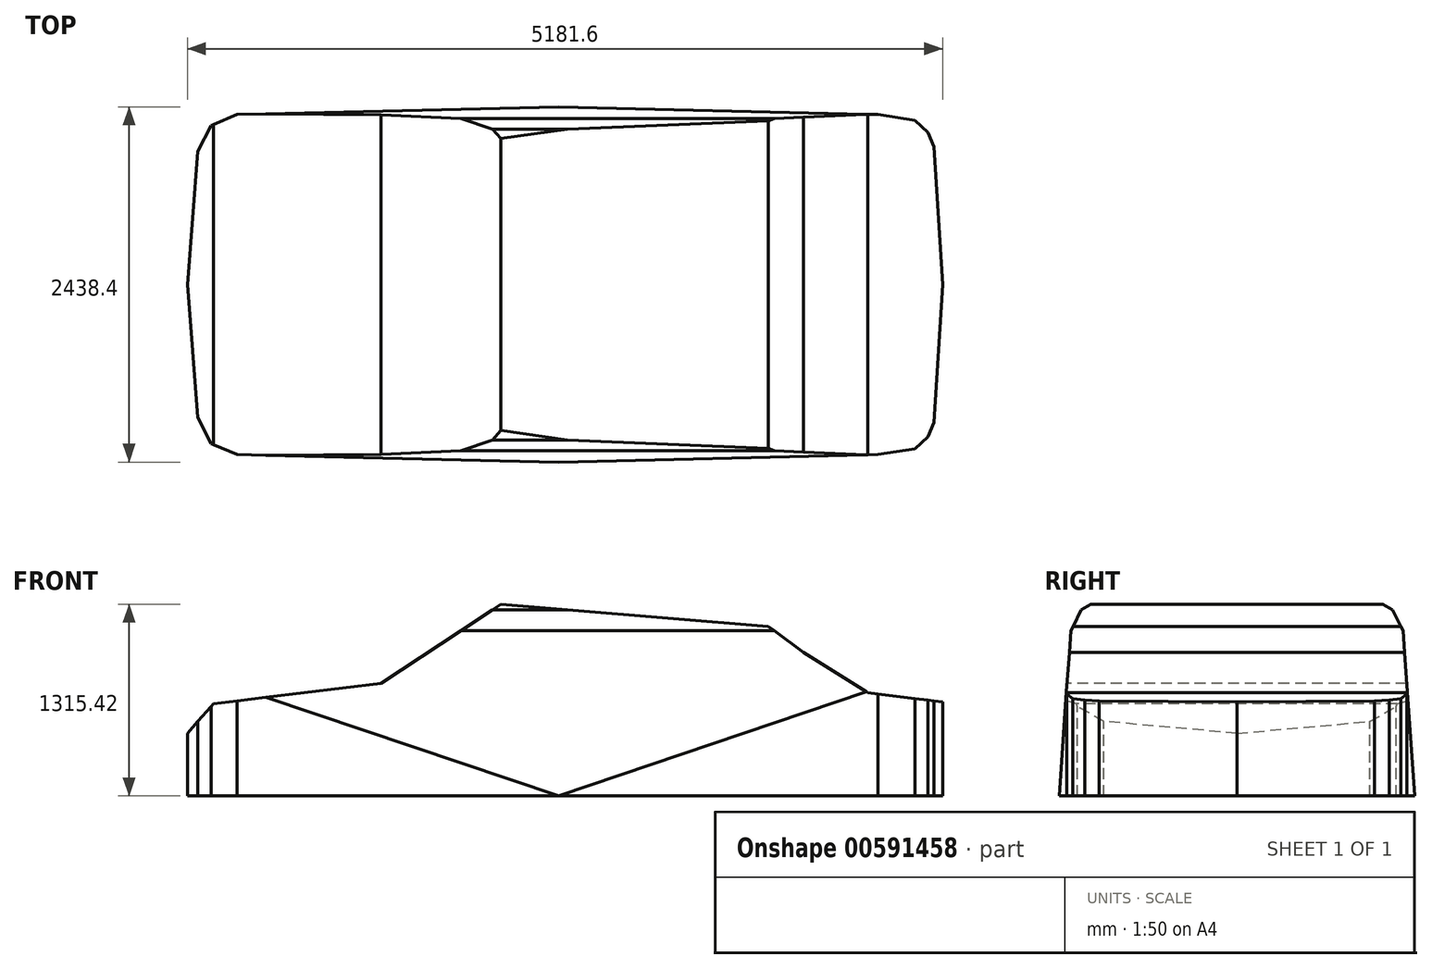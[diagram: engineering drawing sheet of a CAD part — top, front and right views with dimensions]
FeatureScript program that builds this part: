
annotation { "Feature Type Name" : "Feature", "Feature Type Description" : "" }
export const myFeature = defineFeature(function(context is Context, id is Id, definition is map)
    precondition{}
    {
        {
            var Q0;
            Q0=qCreatedBy(makeId("Top.planeOp"),FACE);
            var sketch = newSketch(context, id + "F0", { "sketchPlane" : qUnion([Q0])});
            skLineSegment(sketch, "E0.bottom", {"start": v(-2577.75, 1480) * mm, "end": v(2603.85, 1480) * mm});
            skLineSegment(sketch, "E0.top", {"start": v(-2577.75, -958.4) * mm, "end": v(2603.85, -958.4) * mm});
            skLineSegment(sketch, "E0.left", {"start": v(-2577.75, 1480) * mm, "end": v(-2577.75, -958.4) * mm});
            skLineSegment(sketch, "E0.right", {"start": v(2603.85, 1480) * mm, "end": v(2603.85, -958.4) * mm});
            skSolve(sketch);
        }
        {
            var Q0;
            Q0=makeQuery(id+"F0.imprint","IMPRINT",FACE,{"disambiguationData":[TD([[makeQuery(id+"F0.imprint","IMPRINT",EDGE,{"derivedFrom":sQuery(id+"F0.wireOp",EDGE,"E0.bottom")}),-1.0]])]});
            extrude(context, id + "F1", {"entities" : qUnion([Q0]), "depth" : 1524 * mm, "offsetDistance" : 25.4 * mm});
        }
        {
            var Q0;
            Q0=makeQuery(id+"F1.opExtrude","SWEPT_FACE",FACE,{"disambiguationData":[OSD([sQuery(id+"F0.wireOp",EDGE,"E0.top")])]});
            var sketch = newSketch(context, id + "F2", { "sketchPlane" : qUnion([Q0])});
            skLineSegment(sketch, "E1", {"start": v(2603.85, 644.82) * mm, "end": v(2603.85, 0) * mm});
            skLineSegment(sketch, "E2", {"start": v(2603.85, 0) * mm, "end": v(-2577.75, 0) * mm});
            skLineSegment(sketch, "E3", {"start": v(-2577.75, 0) * mm, "end": v(-2577.75, 429.72) * mm});
            skLineSegment(sketch, "E4", {"start": v(-2577.75, 429.72) * mm, "end": v(-2400.46, 632.17) * mm});
            skLineSegment(sketch, "E5", {"start": v(-2400.46, 632.17) * mm, "end": v(-1249.06, 771.35) * mm});
            skLineSegment(sketch, "E6", {"start": v(-1249.06, 771.35) * mm, "end": v(-426.63, 1315.42) * mm});
            skLineSegment(sketch, "E7", {"start": v(-426.63, 1315.42) * mm, "end": v(1408.01, 1163.58) * mm});
            skLineSegment(sketch, "E8", {"start": v(1408.01, 1163.58) * mm, "end": v(1648.42, 986.44) * mm});
            skLineSegment(sketch, "E9", {"start": v(1648.42, 986.44) * mm, "end": v(2091.26, 708.08) * mm});
            skLineSegment(sketch, "E10", {"start": v(2091.26, 708.08) * mm, "end": v(2603.85, 644.82) * mm});
            skLineSegment(sketch, "E11.bottom", {"start": v(3070.3, 1751.39) * mm, "end": v(-2943.02, 1751.39) * mm});
            skLineSegment(sketch, "E11.top", {"start": v(3070.3, -470.59) * mm, "end": v(-2943.02, -470.59) * mm});
            skLineSegment(sketch, "E11.left", {"start": v(3070.3, 1751.39) * mm, "end": v(3070.3, -470.59) * mm});
            skLineSegment(sketch, "E11.right", {"start": v(-2943.02, 1751.39) * mm, "end": v(-2943.02, -470.59) * mm});
            skSolve(sketch);
        }
        {
            var Q0;
            Q0=makeQuery(id+"F1.opExtrude","CAP_FACE",FACE,{"disambiguationData":[OSD([sQuery(id+"F0.wireOp",EDGE,"E0.bottom"),sQuery(id+"F0.wireOp",EDGE,"E0.top"),sQuery(id+"F0.wireOp",EDGE,"E0.left"),sQuery(id+"F0.wireOp",EDGE,"E0.right")])],"isStart":false});
            var sketch = newSketch(context, id + "F3", { "sketchPlane" : qUnion([Q0])});
            skLineSegment(sketch, "E12", {"start": v(2603.85, 260.8) * mm, "end": v(2544.85, 1206.36) * mm});
            skLineSegment(sketch, "E13", {"start": v(2544.85, 1206.36) * mm, "end": v(2503.83, 1304.8) * mm});
            skLineSegment(sketch, "E14", {"start": v(2503.83, 1304.8) * mm, "end": v(2413.58, 1386.85) * mm});
            skLineSegment(sketch, "E15", {"start": v(2413.58, 1386.85) * mm, "end": v(2159.25, 1427.87) * mm});
            skLineSegment(sketch, "E16", {"start": v(2159.25, 1427.87) * mm, "end": v(-29.95, 1480) * mm});
            skLineSegment(sketch, "E17", {"start": v(-29.95, 1480) * mm, "end": v(-2235.72, 1427.87) * mm});
            skLineSegment(sketch, "E18", {"start": v(-2235.72, 1427.87) * mm, "end": v(-2416.21, 1353.9) * mm});
            skLineSegment(sketch, "E19", {"start": v(-2416.21, 1353.9) * mm, "end": v(-2506.46, 1173.41) * mm});
            skLineSegment(sketch, "E20", {"start": v(-2506.46, 1173.41) * mm, "end": v(-2577.75, 260.8) * mm});
            skLineSegment(sketch, "E21.MirrorCS", {"start": v(2413.58, -865.26) * mm, "end": v(2159.25, -906.28) * mm});
            skLineSegment(sketch, "E22.MirrorCS", {"start": v(2503.83, -783.21) * mm, "end": v(2413.58, -865.26) * mm});
            skLineSegment(sketch, "E23.MirrorCS", {"start": v(2544.85, -684.76) * mm, "end": v(2503.83, -783.21) * mm});
            skLineSegment(sketch, "E24.MirrorCS", {"start": v(-2416.21, -832.3) * mm, "end": v(-2506.46, -651.82) * mm});
            skLineSegment(sketch, "E25.MirrorCS", {"start": v(-2235.72, -906.28) * mm, "end": v(-2416.21, -832.3) * mm});
            skLineSegment(sketch, "E26.MirrorCS", {"start": v(-2506.46, -651.82) * mm, "end": v(-2577.75, 260.8) * mm});
            skLineSegment(sketch, "E27.MirrorCS", {"start": v(2159.25, -906.28) * mm, "end": v(-29.95, -958.4) * mm});
            skLineSegment(sketch, "E28.MirrorCS", {"start": v(2603.85, 260.8) * mm, "end": v(2544.85, -684.76) * mm});
            skLineSegment(sketch, "E29.MirrorCS", {"start": v(-29.95, -958.4) * mm, "end": v(-2235.72, -906.28) * mm});
            skLineSegment(sketch, "E30.bottom", {"start": v(-3175.93, 1909.52) * mm, "end": v(3232.7, 1909.52) * mm});
            skLineSegment(sketch, "E30.top", {"start": v(-3175.93, -1419.34) * mm, "end": v(3232.7, -1419.34) * mm});
            skLineSegment(sketch, "E30.left", {"start": v(-3175.93, 1909.52) * mm, "end": v(-3175.93, -1419.34) * mm});
            skLineSegment(sketch, "E30.right", {"start": v(3232.7, 1909.52) * mm, "end": v(3232.7, -1419.34) * mm});
            skSolve(sketch);
        }
        {
            var Q0;
            Q0 = qSketchRegion(id + "F2", true);
            extrude(context, id + "F4", {"entities" : qUnion([Q0]), "operationType" : NewBodyOperationType.REMOVE, "endBound" : BoundingType.THROUGH_ALL, "oppositeDirection" : true, "depth" : 25.4 * mm, "offsetDistance" : 25.4 * mm});
        }
        {
            var Q0;
            Q0 = qSketchRegion(id + "F3", true);
            extrude(context, id + "F5", {"entities" : qUnion([Q0]), "operationType" : NewBodyOperationType.REMOVE, "endBound" : BoundingType.THROUGH_ALL, "oppositeDirection" : true, "depth" : 25.4 * mm, "offsetDistance" : 25.4 * mm});
        }
        {
            var Q0;
            Q0=qCreatedBy(makeId("Right.planeOp"),FACE);
            var sketch = newSketch(context, id + "F6", { "sketchPlane" : qUnion([Q0])});
            skLineSegment(sketch, "E31", {"start": v(-958.4, 0) * mm, "end": v(-878.66, 1133.59) * mm});
            skLineSegment(sketch, "E32", {"start": v(-878.66, 1133.59) * mm, "end": v(-806.6, 1277.72) * mm});
            skLineSegment(sketch, "E33", {"start": v(-806.6, 1277.72) * mm, "end": v(-617.43, 1385.81) * mm});
            skLineSegment(sketch, "E34", {"start": v(-617.43, 1385.81) * mm, "end": v(-145.07, 1499.75) * mm});
            skLineSegment(sketch, "E35", {"start": v(-145.07, 1499.75) * mm, "end": v(260.8, 1524) * mm});
            skLineSegment(sketch, "E36", {"start": v(260.8, 0) * mm, "end": v(-958.4, 0) * mm});
            skLineSegment(sketch, "E37.MirrorCS", {"start": v(1480, 0) * mm, "end": v(1400.26, 1133.59) * mm});
            skLineSegment(sketch, "E38.MirrorCS", {"start": v(1400.26, 1133.59) * mm, "end": v(1328.2, 1277.72) * mm});
            skLineSegment(sketch, "E39.MirrorCS", {"start": v(1328.2, 1277.72) * mm, "end": v(1139.02, 1385.81) * mm});
            skLineSegment(sketch, "E40.MirrorCS", {"start": v(666.66, 1499.75) * mm, "end": v(260.8, 1524) * mm});
            skLineSegment(sketch, "E41.MirrorCS", {"start": v(1139.02, 1385.81) * mm, "end": v(666.66, 1499.75) * mm});
            skLineSegment(sketch, "E42.bottom", {"start": v(-1677.32, 1819.9) * mm, "end": v(2268.07, 1819.9) * mm});
            skLineSegment(sketch, "E42.top", {"start": v(-1677.32, -388.97) * mm, "end": v(2268.07, -388.97) * mm});
            skLineSegment(sketch, "E42.left", {"start": v(-1677.32, 1819.9) * mm, "end": v(-1677.32, -388.97) * mm});
            skLineSegment(sketch, "E42.right", {"start": v(2268.07, 1819.9) * mm, "end": v(2268.07, -388.97) * mm});
            skLineSegment(sketch, "E43", {"start": v(260.8, 0) * mm, "end": v(1480, 0) * mm});
            skSolve(sketch);
        }
        {
            var Q0;
            Q0 = qSketchRegion(id + "F6", true);
            extrude(context, id + "F7", {"entities" : qUnion([Q0]), "operationType" : NewBodyOperationType.REMOVE, "endBound" : BoundingType.SYMMETRIC, "oppositeDirection" : true, "depth" : 25400 * mm, "offsetDistance" : 25.4 * mm});
        }
    });
